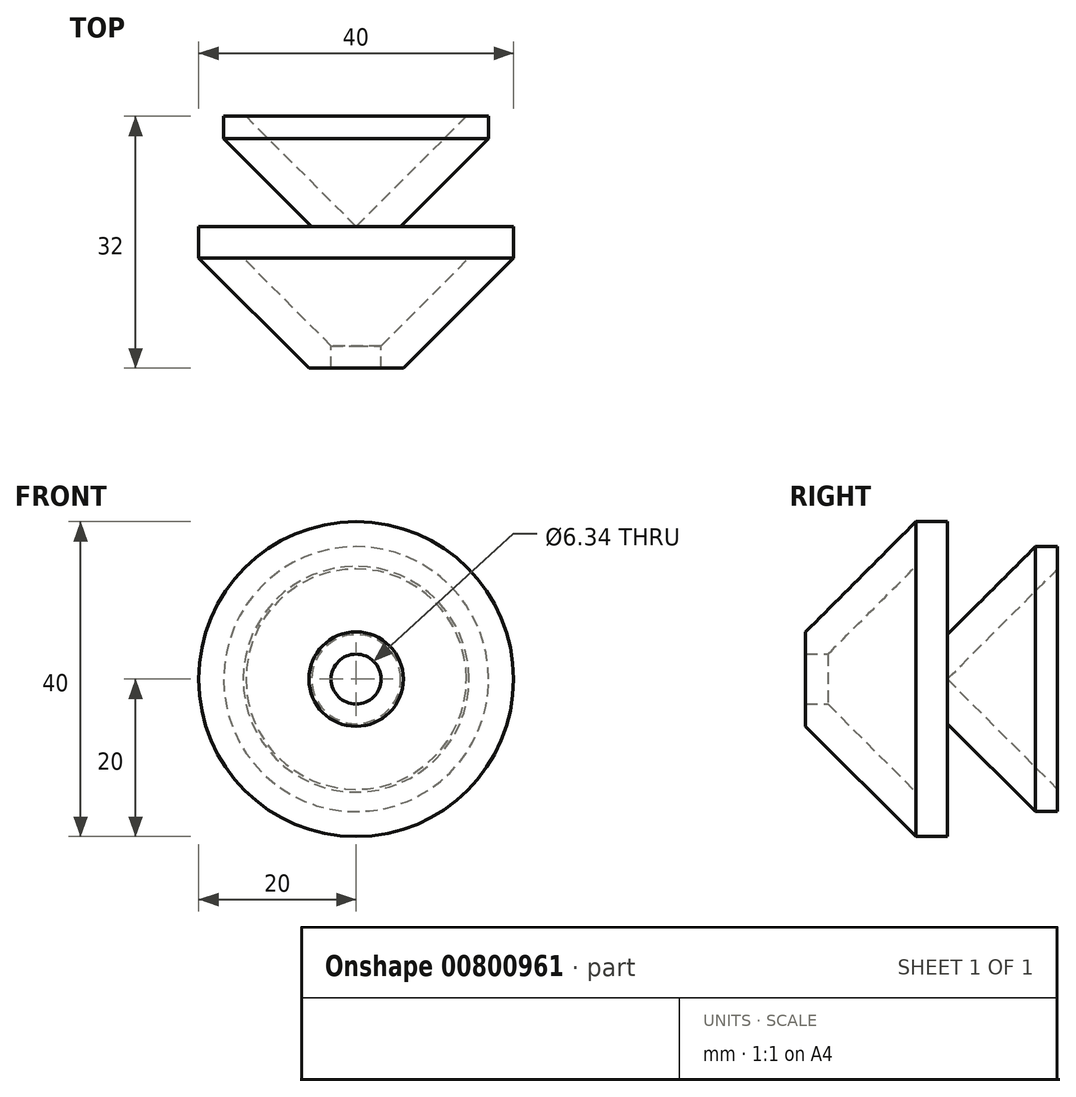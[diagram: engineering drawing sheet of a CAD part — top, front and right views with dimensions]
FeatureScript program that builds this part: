
annotation { "Feature Type Name" : "Feature", "Feature Type Description" : "" }
export const myFeature = defineFeature(function(context is Context, id is Id, definition is map)
    precondition{}
    {
        {
            var Q0;
            Q0=qCreatedBy(makeId("Top.planeOp"),FACE);
            var sketch = newSketch(context, id + "F0", { "sketchPlane" : qUnion([Q0])});
            skLineSegment(sketch, "E0", {"start": v(16.83, 0) * mm, "end": v(14, 0) * mm});
            skLineSegment(sketch, "E1", {"start": v(14, 0) * mm, "end": v(0, -14) * mm});
            skLineSegment(sketch, "E2", {"start": v(0, -14) * mm, "end": v(0, -18) * mm});
            skLineSegment(sketch, "E3", {"start": v(0, -18) * mm, "end": v(14.34, -18) * mm});
            skLineSegment(sketch, "E4", {"start": v(20, -14) * mm, "end": v(5.66, -14) * mm});
            skLineSegment(sketch, "E5", {"start": v(5.66, -14) * mm, "end": v(16.83, -2.83) * mm});
            skLineSegment(sketch, "E6", {"start": v(16.83, -2.83) * mm, "end": v(16.83, 0) * mm});
            skLineSegment(sketch, "E7", {"start": v(6, -32) * mm, "end": v(20, -18) * mm});
            skLineSegment(sketch, "E8", {"start": v(20, -18) * mm, "end": v(20, -14) * mm});
            skLineSegment(sketch, "E9", {"start": v(14.34, -18) * mm, "end": v(20, -18) * mm, "construction": true});
            skLineSegment(sketch, "E10", {"start": v(6, -32) * mm, "end": v(3.17, -32) * mm});
            skLineSegment(sketch, "E11", {"start": v(3.17, -32) * mm, "end": v(3.17, -29.17) * mm});
            skLineSegment(sketch, "E12", {"start": v(3.17, -29.17) * mm, "end": v(14.34, -18) * mm});
            skSolve(sketch);
        }
        {
            var Q0;
            Q0=makeQuery(id+"F0.imprint","IMPRINT",FACE,{"disambiguationData":[TD([[makeQuery(id+"F0.imprint","IMPRINT",EDGE,{"derivedFrom":sQuery(id+"F0.wireOp",EDGE,"E0")}),1.0]])]});
            var Q1;
            Q1=sQuery(id+"F0.wireOp",EDGE,"E2");
            revolve(context, id + "F1", {"surfaceOperationType" : NewSurfaceOperationType.NEW, "entities" : qUnion([Q0]), "axis" : qUnion([Q1]), "revolveType" : RevolveType.FULL});
        }
    });
